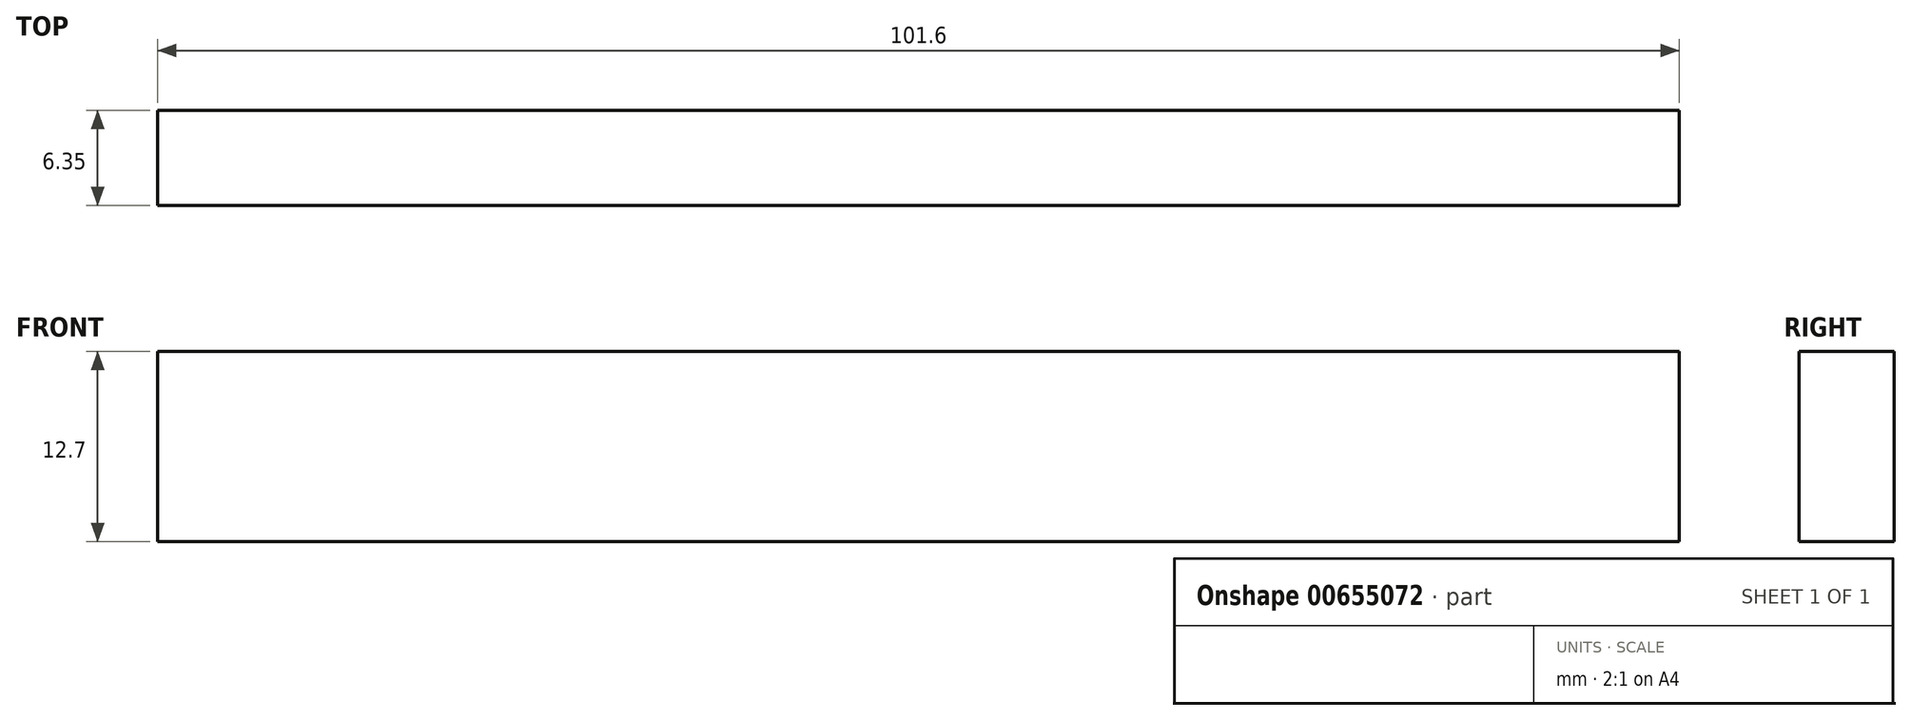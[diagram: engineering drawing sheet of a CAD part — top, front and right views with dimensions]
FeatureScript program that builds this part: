
annotation { "Feature Type Name" : "Feature", "Feature Type Description" : "" }
export const myFeature = defineFeature(function(context is Context, id is Id, definition is map)
    precondition{}
    {
        {
            var Q0;
            Q0=qCreatedBy(makeId("Front.planeOp"),FACE);
            var sketch = newSketch(context, id + "F0", { "sketchPlane" : qUnion([Q0])});
            skLineSegment(sketch, "E0.bottom", {"start": v(-50.8, 6.35) * mm, "end": v(50.8, 6.35) * mm});
            skLineSegment(sketch, "E0.top", {"start": v(-50.8, -6.35) * mm, "end": v(50.8, -6.35) * mm});
            skLineSegment(sketch, "E0.left", {"start": v(-50.8, 6.35) * mm, "end": v(-50.8, -6.35) * mm});
            skLineSegment(sketch, "E0.right", {"start": v(50.8, 6.35) * mm, "end": v(50.8, -6.35) * mm});
            skPoint(sketch, "E0.middle", {"position": v(0, 0) * mm});
            skSolve(sketch);
        }
        {
            var Q0;
            Q0=makeQuery(id+"F0.imprint","IMPRINT",FACE,{"disambiguationData":[TD([[makeQuery(id+"F0.imprint","IMPRINT",EDGE,{"derivedFrom":sQuery(id+"F0.wireOp",EDGE,"E0.bottom")}),-1.0]])]});
            extrude(context, id + "F1", {"entities" : qUnion([Q0]), "oppositeDirection" : true, "depth" : 6.35 * mm, "offsetDistance" : 25.4 * mm});
        }
    });
